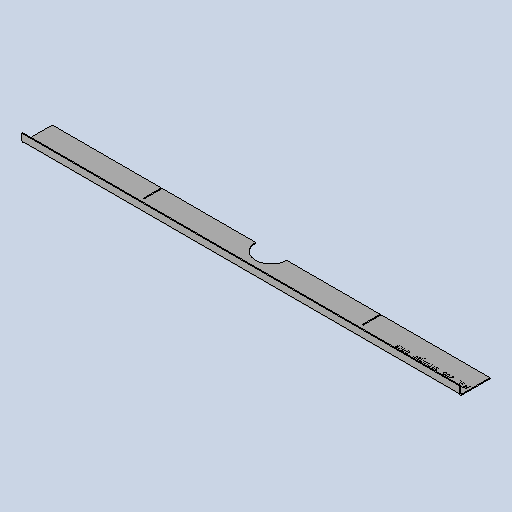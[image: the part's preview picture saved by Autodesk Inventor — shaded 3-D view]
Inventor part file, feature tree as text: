
AUTODESK INVENTOR PART (.ipt)
format: ipt  version: 2025 (Build 290162010, 162A)  size: 264,192 bytes
history: native  units: mm
features: other x5, sheet_metal_op x4, sketch x4, extrude x1
ambient origin geometry x8: Origin, YZ Plane, XZ Plane, XY Plane, X Axis, Y Axis, Z Axis, Center Point
bodies: Solid1 (feature_tree)
feature tree (14):
  sheet_metal_op  "Face1"
  sheet_metal_op  "Flange1"
  extrude  "Extrusion1"  Depth=68.0mm
  other  "Mark2"
  other  "A-Side Definition"
  sketch  "Sketch1"  dims[d0=980.0mm d1=68.0mm]
  other  "Plate1"
  sketch  "Sketch2"  dims[d2=2.0mm]
  other  "Plate2"
  sheet_metal_op  "Bend1"
  sheet_metal_op  "Corner1"
  sketch  "Sketch5"  dims[d3=2.0mm]
  sketch  "Sketch9"  dims[d4=1.0mm d5=4.0mm d6=2.75mm d7=20.0mm d8=90.0deg d9=2.75mm d10=8.0mm d11=2.0mm d12=2.75mm d15=0.0mm d16=0.0mm d40=200.0mm d41=12.0mm d45=70.0mm d48=2.1mm d49=490.0mm d51=29.0mm d52=39.0mm]
  other  "Definition1"
